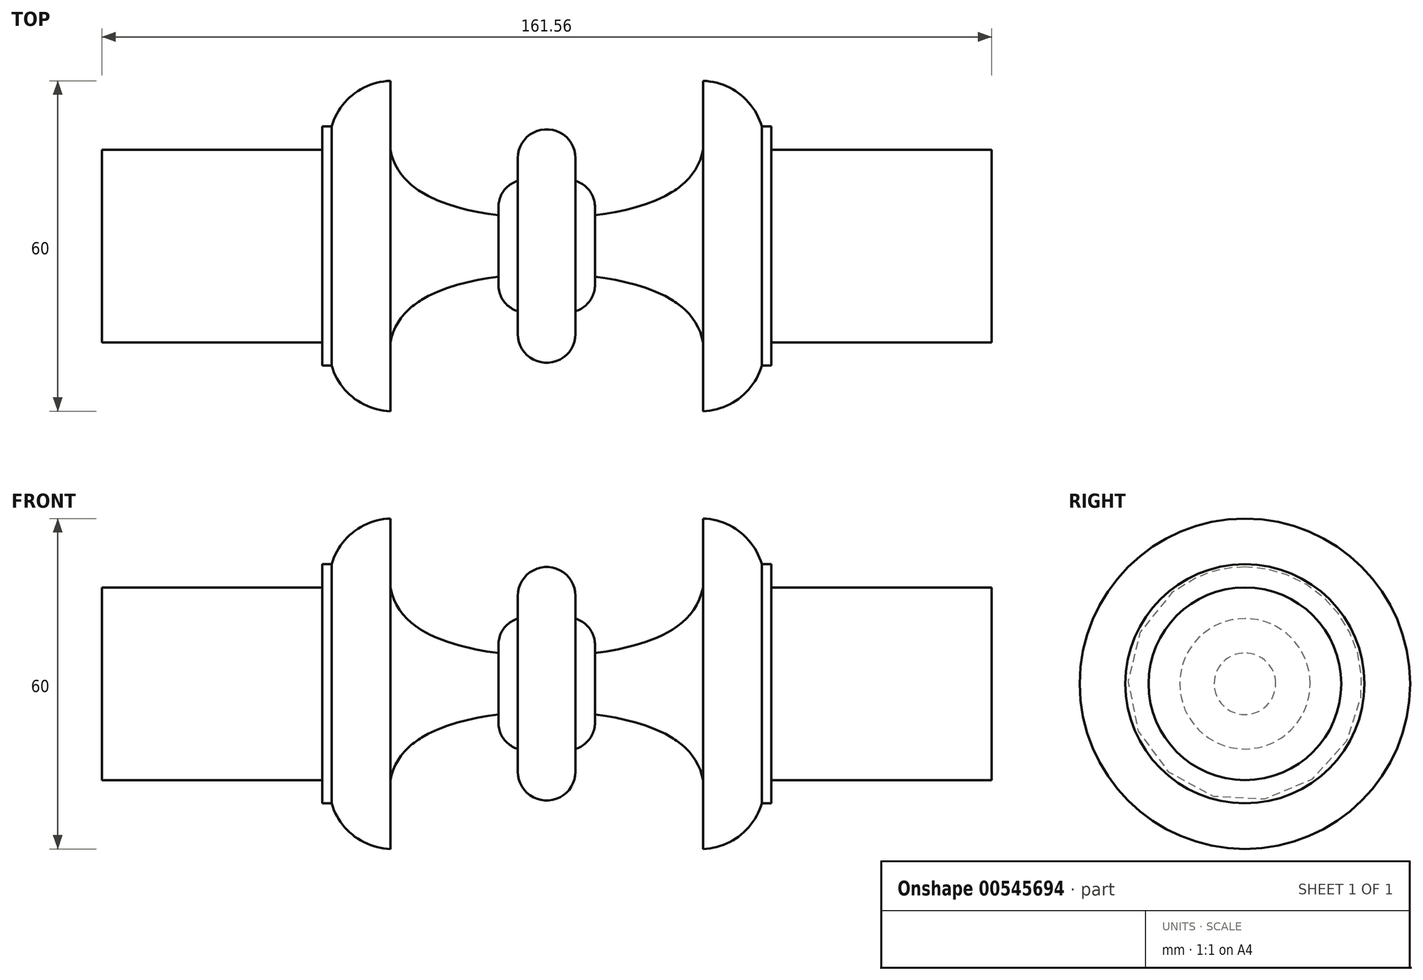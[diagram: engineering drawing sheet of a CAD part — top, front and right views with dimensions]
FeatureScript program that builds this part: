
annotation { "Feature Type Name" : "Feature", "Feature Type Description" : "" }
export const myFeature = defineFeature(function(context is Context, id is Id, definition is map)
    precondition{}
    {
        {
            var Q0;
            Q0=qCreatedBy(makeId("Front.planeOp"),FACE);
            var sketch = newSketch(context, id + "F0", { "sketchPlane" : qUnion([Q0])});
            skLineSegment(sketch, "E0", {"start": v(0, 0) * mm, "end": v(80.78, 0) * mm});
            skLineSegment(sketch, "E1", {"start": v(80.78, 0) * mm, "end": v(80.78, 17.5) * mm});
            skLineSegment(sketch, "E2", {"start": v(0, 0) * mm, "end": v(0, 5.23) * mm});
            skLineSegment(sketch, "E3", {"start": v(39.05, 17.5) * mm, "end": v(39.05, 21.7) * mm});
            skLineSegment(sketch, "E4", {"start": v(28.4, 30) * mm, "end": v(28.4, 17.5) * mm});
            skFitSpline(sketch, "E5", {"points": [v(28.4, 17.5) * mm, v(16.55, 7.16) * mm, v(0, 5.23) * mm], "startDerivative": vector(-7.28, -36.88) * mm, "endDerivative": vector(-33.63, 0.65) * mm});
            skLineSegment(sketch, "E6", {"start": v(39.05, 21.7) * mm, "end": v(40.78, 21.7) * mm});
            skLineSegment(sketch, "E7", {"start": v(40.78, 21.7) * mm, "end": v(40.78, 17.5) * mm});
            skLineSegment(sketch, "E8", {"start": v(39.05, 17.5) * mm, "end": v(80.78, 17.5) * mm});
            skLineSegment(sketch, "E9", {"start": v(0, 0) * mm, "end": v(0, 15.97) * mm});
            skLineSegment(sketch, "E10", {"start": v(0, 15.97) * mm, "end": v(5.23, 15.97) * mm});
            skLineSegment(sketch, "E11", {"start": v(5.23, 15.97) * mm, "end": v(5.23, 0) * mm});
            skLineSegment(sketch, "E12", {"start": v(5.23, 0) * mm, "end": v(0, 0) * mm});
            skLineSegment(sketch, "E13", {"start": v(5.23, 11.84) * mm, "end": v(8.77, 11.84) * mm});
            skLineSegment(sketch, "E14", {"start": v(8.77, 11.84) * mm, "end": v(8.77, 0) * mm});
            skLineSegment(sketch, "E15", {"start": v(8.77, 0) * mm, "end": v(5.23, 0) * mm});
            skArc(sketch, "E16", {"start": v(39.05, 21.7) * mm, "mid": v(35.07, 27.58) * mm, "end": v(28.4, 30) * mm});
            skArc(sketch, "E17", {"start": v(5.23, 15.97) * mm, "mid": v(3.7, 19.67) * mm, "end": v(0, 21.2) * mm});
            skLineSegment(sketch, "E18", {"start": v(0, 15.97) * mm, "end": v(0, 21.2) * mm});
            skSolve(sketch);
        }
        {
            var Q0;
            Q0 = qSketchRegion(id + "F0", true);
            var Q1;
            Q1=sQuery(id+"F0.wireOp",EDGE,"E0");
            revolve(context, id + "F1", {"entities" : qUnion([Q0]), "axis" : qUnion([Q1]), "revolveType" : RevolveType.FULL});
        }
        {
            var Q0;
            Q0=makeQuery(id+"F1.opRevolve","SWEPT_BODY",BODY,{"disambiguationData":[OSD([sQuery(id+"F0.wireOp",EDGE,"E0"),sQuery(id+"F0.wireOp",EDGE,"E1"),sQuery(id+"F0.wireOp",EDGE,"rtAyOKtI-6zbg-A1Fw-FdDm-gOTqnAeZi8pi"),sQuery(id+"F0.wireOp",EDGE,"E2"),sQuery(id+"F0.wireOp",EDGE,"E3"),sQuery(id+"F0.wireOp",EDGE,"WwwCh2EO-enQK-hj5b-BqjA-qWZrKvvLJaLe"),sQuery(id+"F0.wireOp",EDGE,"E4"),sQuery(id+"F0.wireOp",EDGE,"E5")])]});
            var Q1;
            Q1=qCreatedBy(makeId("Right.planeOp"),FACE);
            mirror(context, id + "F2", {"operationType" : NewBodyOperationType.ADD, "entities" : qUnion([Q0]), "mirrorPlane" : qUnion([Q1])});
        }
        {
            var Q0;
            Q0=makeQuery(id+"F1.opRevolve","SWEPT_EDGE",EDGE,{"disambiguationData":[OSD([sQuery(id+"F0.wireOp",EDGE,"E13"),sQuery(id+"F0.wireOp",EDGE,"E14")])]});
            var Q1;
            Q1=makeQuery(id+"F2.opPattern","COPY",EDGE,{"derivedFrom":makeQuery(id+"F1.opRevolve","SWEPT_EDGE",EDGE,{"disambiguationData":[OSD([sQuery(id+"F0.wireOp",EDGE,"E13"),sQuery(id+"F0.wireOp",EDGE,"E14")])]}),"instanceName":"1"});
            fillet(context, id + "F3", {"entities" : qUnion([Q0, Q1]), "radius" : 5 * mm, "tangentPropagation" : true, "allowEdgeOverflow" : false});
        }
    });
